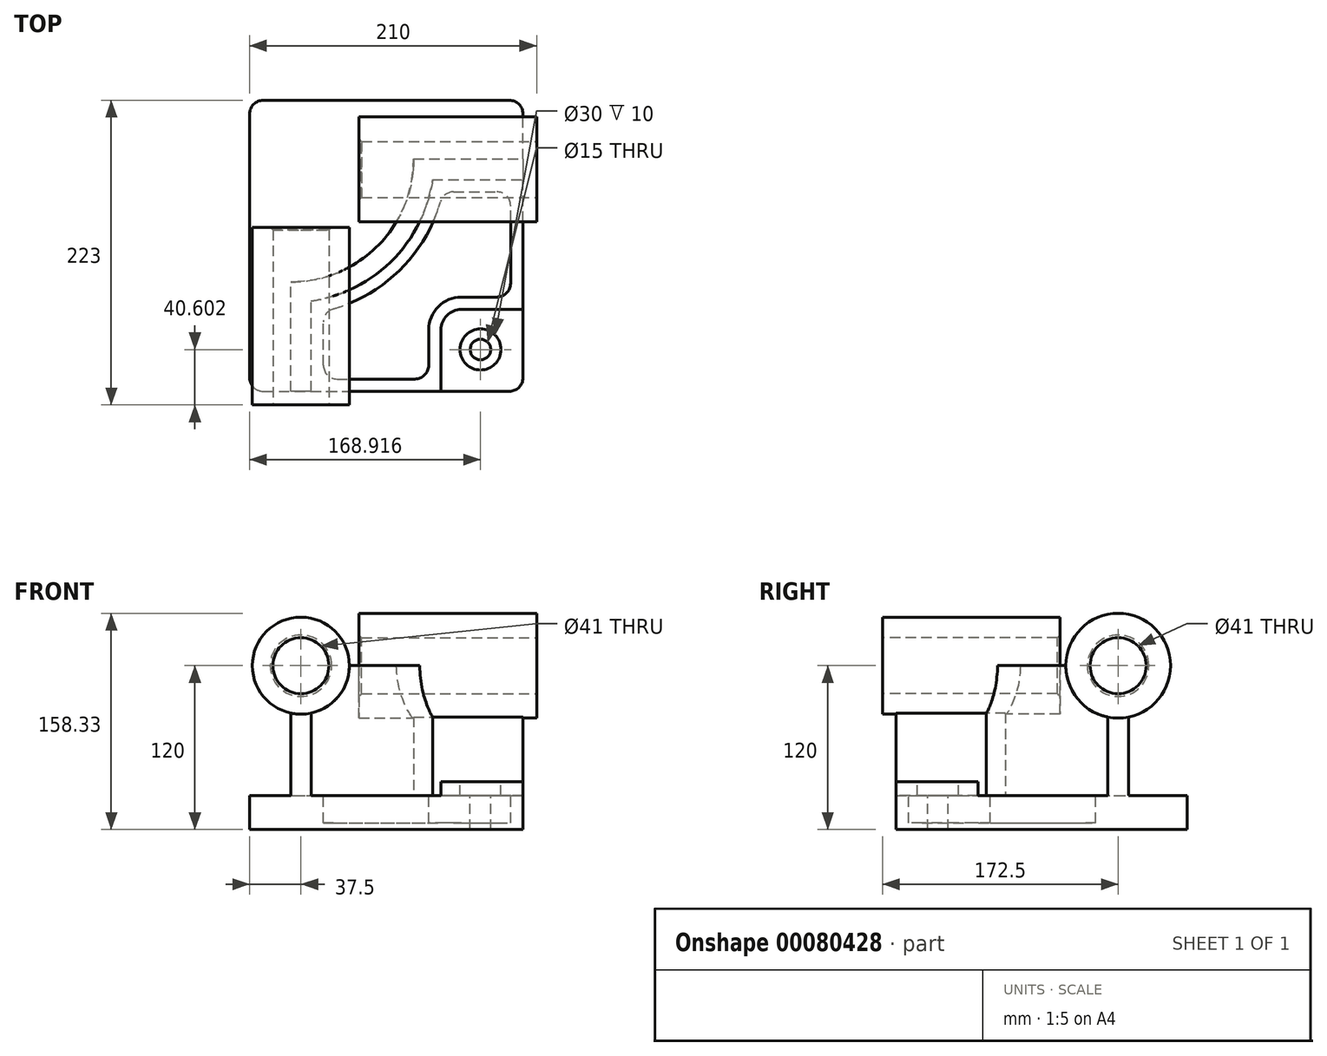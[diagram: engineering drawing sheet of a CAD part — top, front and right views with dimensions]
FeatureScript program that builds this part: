
annotation { "Feature Type Name" : "Feature", "Feature Type Description" : "" }
export const myFeature = defineFeature(function(context is Context, id is Id, definition is map)
    precondition{}
    {
        {
            var Q0;
            Q0=qCreatedBy(makeId("Top.planeOp"),FACE);
            var sketch = newSketch(context, id + "F0", { "sketchPlane" : qUnion([Q0])});
            skLineSegment(sketch, "E0.bottom", {"start": v(0, 0) * mm, "end": v(200, 0) * mm});
            skLineSegment(sketch, "E0.top", {"start": v(0, 213) * mm, "end": v(200, 213) * mm});
            skLineSegment(sketch, "E0.left", {"start": v(0, 0) * mm, "end": v(0, 213) * mm});
            skLineSegment(sketch, "E0.right", {"start": v(200, 0) * mm, "end": v(200, 213) * mm});
            skSolve(sketch);
        }
        {
            var Q0;
            Q0 = qSketchRegion(id + "F0", true);
            extrude(context, id + "F1", {"entities" : qUnion([Q0]), "depth" : 25 * mm});
        }
        {
            var Q0;
            Q0=makeQuery(id+"F1.opExtrude","CAP_FACE",FACE,{"disambiguationData":[OSD([sQuery(id+"F0.wireOp",EDGE,"E0.bottom"),sQuery(id+"F0.wireOp",EDGE,"E0.top"),sQuery(id+"F0.wireOp",EDGE,"E0.left"),sQuery(id+"F0.wireOp",EDGE,"E0.right")])],"isStart":false});
            var sketch = newSketch(context, id + "F2", { "sketchPlane" : qUnion([Q0])});
            skLineSegment(sketch, "E1", {"start": v(30, 0) * mm, "end": v(30, 80) * mm});
            skLineSegment(sketch, "E2", {"start": v(30, 0) * mm, "end": v(45, 0) * mm});
            skLineSegment(sketch, "E3", {"start": v(45, 0) * mm, "end": v(45, 66.08) * mm});
            skLineSegment(sketch, "E4", {"start": v(120, 170) * mm, "end": v(200, 170) * mm});
            skLineSegment(sketch, "E5", {"start": v(133.92, 155) * mm, "end": v(200, 155) * mm});
            skLineSegment(sketch, "E6", {"start": v(200, 155) * mm, "end": v(200, 170) * mm});
            skArc(sketch, "E7", {"start": v(30, 80) * mm, "mid": v(93.64, 106.36) * mm, "end": v(120, 170) * mm});
            skArc(sketch, "E8", {"start": v(45, 66.08) * mm, "mid": v(104.25, 95.75) * mm, "end": v(133.92, 155) * mm});
            skSolve(sketch);
        }
        {
            var Q0;
            Q0 = qSketchRegion(id + "F2", true);
            extrude(context, id + "F3", {"entities" : qUnion([Q0]), "operationType" : NewBodyOperationType.ADD, "depth" : 95 * mm});
        }
        {
            var Q0;
            {var subQ0=sQuery(id+"F0.wireOp",EDGE,"E0.right");var subQ1=sQuery(id+"F0.wireOp",EDGE,"E0.bottom");Q0=makeQuery(id+"F3.boolean.opBoolean","SPLIT",FACE,{"disambiguationData":[TD([makeQuery(id+"F3.opExtrude","SWEPT_FACE",FACE,{"disambiguationData":[OSD([sQuery(id+"F2.wireOp",EDGE,"E3")])]})])],"derivedFrom":makeQuery(id+"F1.opExtrude","CAP_FACE",FACE,{"disambiguationData":[OSD([subQ1,sQuery(id+"F0.wireOp",EDGE,"E0.top"),sQuery(id+"F0.wireOp",EDGE,"E0.left"),subQ0])],"isStart":false})});}
            var sketch = newSketch(context, id + "F4", { "sketchPlane" : qUnion([Q0])});
            skLineSegment(sketch, "E9.bottom", {"start": v(155, 60) * mm, "end": v(200, 60) * mm});
            skLineSegment(sketch, "E9.top", {"start": v(140, 0) * mm, "end": v(200, 0) * mm});
            skLineSegment(sketch, "E9.left", {"start": v(140, 45) * mm, "end": v(140, 0) * mm});
            skLineSegment(sketch, "E9.right", {"start": v(200, 60) * mm, "end": v(200, 0) * mm});
            skPoint(sketch, "E10.visualSharp", {"position": v(140, 60) * mm});
            skArc(sketch, "E10.filletArc", {"start": v(155, 60) * mm, "mid": v(144.4, 55.6) * mm, "end": v(140, 45) * mm});
            skSolve(sketch);
        }
        {
            var Q0;
            Q0 = qSketchRegion(id + "F4", true);
            extrude(context, id + "F5", {"entities" : qUnion([Q0]), "operationType" : NewBodyOperationType.ADD, "depth" : 10 * mm});
        }
        {
            var Q0;
            Q0=makeQuery(id+"F5.opExtrude","CAP_FACE",FACE,{"disambiguationData":[OSD([sQuery(id+"F4.wireOp",EDGE,"E9.bottom"),sQuery(id+"F4.wireOp",EDGE,"E9.top"),sQuery(id+"F4.wireOp",EDGE,"E9.left"),sQuery(id+"F4.wireOp",EDGE,"E9.right"),sQuery(id+"F4.wireOp",EDGE,"E10.filletArc")])],"isStart":false});
            var sketch = newSketch(context, id + "F6", { "sketchPlane" : qUnion([Q0])});
            skCircle(sketch, "E11", {"center": v(168.92, 30.6) * mm, "radius": 15 * mm});
            skSolve(sketch);
        }
        {
            var Q0;
            Q0 = qSketchRegion(id + "F6", true);
            extrude(context, id + "F7", {"entities" : qUnion([Q0]), "operationType" : NewBodyOperationType.REMOVE, "oppositeDirection" : true, "depth" : 10 * mm});
        }
        {
            var Q0;
            Q0=makeQuery(id+"F7.boolean.opBoolean","COPY",FACE,{"derivedFrom":makeQuery(id+"F7.opExtrude","CAP_FACE",FACE,{"disambiguationData":[OSD([sQuery(id+"F6.wireOp",EDGE,"E11")])],"isStart":false})});
            var sketch = newSketch(context, id + "F8", { "sketchPlane" : qUnion([Q0])});
            skCircle(sketch, "E12", {"center": v(168.92, 30.6) * mm, "radius": 7.5 * mm});
            skSolve(sketch);
        }
        {
            var Q0;
            Q0 = qSketchRegion(id + "F8", true);
            extrude(context, id + "F9", {"entities" : qUnion([Q0]), "operationType" : NewBodyOperationType.REMOVE, "endBound" : BoundingType.THROUGH_ALL, "oppositeDirection" : true, "depth" : 25 * mm});
        }
        {
            var Q0;
            {var subQ0=sQuery(id+"F0.wireOp",EDGE,"E0.right");var subQ1=sQuery(id+"F0.wireOp",EDGE,"E0.bottom");Q0=makeQuery(id+"F3.boolean.opBoolean","SPLIT",FACE,{"disambiguationData":[TD([makeQuery(id+"F3.opExtrude","SWEPT_FACE",FACE,{"disambiguationData":[OSD([sQuery(id+"F2.wireOp",EDGE,"E3")])]})])],"derivedFrom":makeQuery(id+"F1.opExtrude","CAP_FACE",FACE,{"disambiguationData":[OSD([subQ1,sQuery(id+"F0.wireOp",EDGE,"E0.top"),sQuery(id+"F0.wireOp",EDGE,"E0.left"),subQ0])],"isStart":false})});}
            var sketch = newSketch(context, id + "F10", { "sketchPlane" : qUnion([Q0])});
            skLineSegment(sketch, "E13.0", {"start": v(149.25, 146) * mm, "end": v(181, 146) * mm});
            skArc(sketch, "E13.1", {"start": v(61.26, 60.37) * mm, "mid": v(110.61, 89.39) * mm, "end": v(139.63, 138.74) * mm});
            skLineSegment(sketch, "E13.2", {"start": v(54, 19) * mm, "end": v(54, 50.75) * mm});
            skLineSegment(sketch, "E14", {"start": v(64, 9) * mm, "end": v(121, 9) * mm});
            skLineSegment(sketch, "E15", {"start": v(191, 79) * mm, "end": v(191, 136) * mm});
            skLineSegment(sketch, "E16.0", {"start": v(155, 69) * mm, "end": v(181, 69) * mm});
            skArc(sketch, "E16.1", {"start": v(155, 69) * mm, "mid": v(138.03, 61.97) * mm, "end": v(131, 45) * mm});
            skLineSegment(sketch, "E16.2", {"start": v(131, 45) * mm, "end": v(131, 19) * mm});
            skPoint(sketch, "E17.visualSharp", {"position": v(54, 58.55) * mm});
            skArc(sketch, "E17.filletArc", {"start": v(61.26, 60.37) * mm, "mid": v(56.02, 56.78) * mm, "end": v(54, 50.75) * mm});
            skPoint(sketch, "E18.visualSharp", {"position": v(54, 9) * mm});
            skArc(sketch, "E18.filletArc", {"start": v(54, 19) * mm, "mid": v(56.93, 11.93) * mm, "end": v(64, 9) * mm});
            skPoint(sketch, "E19.visualSharp", {"position": v(131, 9) * mm});
            skArc(sketch, "E19.filletArc", {"start": v(121, 9) * mm, "mid": v(128.07, 11.93) * mm, "end": v(131, 19) * mm});
            skPoint(sketch, "E20.visualSharp", {"position": v(191, 69) * mm});
            skArc(sketch, "E20.filletArc", {"start": v(181, 69) * mm, "mid": v(188.07, 71.93) * mm, "end": v(191, 79) * mm});
            skPoint(sketch, "E21.visualSharp", {"position": v(191, 146) * mm});
            skArc(sketch, "E21.filletArc", {"start": v(191, 136) * mm, "mid": v(188.07, 143.07) * mm, "end": v(181, 146) * mm});
            skPoint(sketch, "E22.visualSharp", {"position": v(141.45, 146) * mm});
            skArc(sketch, "E22.filletArc", {"start": v(149.25, 146) * mm, "mid": v(143.22, 143.98) * mm, "end": v(139.63, 138.74) * mm});
            skSolve(sketch);
        }
        {
            var Q0;
            Q0 = qSketchRegion(id + "F10", true);
            extrude(context, id + "F11", {"entities" : qUnion([Q0]), "operationType" : NewBodyOperationType.REMOVE, "oppositeDirection" : true, "depth" : 20 * mm});
        }
        {
            var Q0;
            Q0=makeQuery(id+"F5.boolean.opBoolean","MERGE",FACE,{"derivedFrom":[makeQuery(id+"F3.boolean.opBoolean","MERGE",FACE,{"derivedFrom":[makeQuery(id+"F1.opExtrude","SWEPT_FACE",FACE,{"disambiguationData":[OSD([sQuery(id+"F0.wireOp",EDGE,"E0.bottom")])]}),makeQuery(id+"F3.opExtrude","SWEPT_FACE",FACE,{"disambiguationData":[OSD([sQuery(id+"F2.wireOp",EDGE,"E2")])]})]}),makeQuery(id+"F5.opExtrude","SWEPT_FACE",FACE,{"disambiguationData":[OSD([sQuery(id+"F4.wireOp",EDGE,"E9.top")])]})]});
            cPlane(context, id + "F12", {"entities" : qUnion([Q0]), "cplaneType" : CPlaneType.OFFSET, "offset" : 10 * mm, "width" : 150 * mm, "height" : 150 * mm});
        }
        {
            var Q0;
            Q0=qCreatedBy(id+"F12.planeOp",FACE);
            var sketch = newSketch(context, id + "F13", { "sketchPlane" : qUnion([Q0])});
            skCircle(sketch, "E23", {"center": v(37.5, 120) * mm, "radius": 35.5 * mm});
            skSolve(sketch);
        }
        {
            var Q0;
            Q0 = qSketchRegion(id + "F13", true);
            extrude(context, id + "F14", {"entities" : qUnion([Q0]), "operationType" : NewBodyOperationType.ADD, "oppositeDirection" : true, "depth" : 130 * mm});
        }
        {
            var Q0;
            Q0=makeQuery(id+"F13.imprint","IMPRINT",FACE,{"disambiguationData":[TD([[makeQuery(id+"F13.imprint","IMPRINT",EDGE,{"derivedFrom":sQuery(id+"F13.wireOp",EDGE,"E23")}),1.0]])]});
            var sketch = newSketch(context, id + "F15", { "sketchPlane" : qUnion([Q0])});
            skCircle(sketch, "E24", {"center": v(37.5, 120) * mm, "radius": 20.5 * mm});
            skSolve(sketch);
        }
        {
            var Q0;
            Q0 = qSketchRegion(id + "F15", true);
            extrude(context, id + "F16", {"entities" : qUnion([Q0]), "operationType" : NewBodyOperationType.REMOVE, "endBound" : BoundingType.THROUGH_ALL, "oppositeDirection" : true, "depth" : 25 * mm});
        }
        {
            var Q0;
            Q0=makeQuery(id+"F5.boolean.opBoolean","MERGE",FACE,{"derivedFrom":[makeQuery(id+"F3.boolean.opBoolean","MERGE",FACE,{"derivedFrom":[makeQuery(id+"F1.opExtrude","SWEPT_FACE",FACE,{"disambiguationData":[OSD([sQuery(id+"F0.wireOp",EDGE,"E0.right")])]}),makeQuery(id+"F3.opExtrude","SWEPT_FACE",FACE,{"disambiguationData":[OSD([sQuery(id+"F2.wireOp",EDGE,"E6")])]})]}),makeQuery(id+"F5.opExtrude","SWEPT_FACE",FACE,{"disambiguationData":[OSD([sQuery(id+"F4.wireOp",EDGE,"E9.right")])]})]});
            cPlane(context, id + "F17", {"entities" : qUnion([Q0]), "cplaneType" : CPlaneType.OFFSET, "offset" : 10 * mm, "width" : 150 * mm, "height" : 150 * mm});
        }
        {
            var Q0;
            Q0=qCreatedBy(id+"F17.planeOp",FACE);
            var sketch = newSketch(context, id + "F18", { "sketchPlane" : qUnion([Q0])});
            skCircle(sketch, "E25", {"center": v(162.5, 120) * mm, "radius": 38.33 * mm});
            skSolve(sketch);
        }
        {
            var Q0;
            Q0 = qSketchRegion(id + "F18", true);
            extrude(context, id + "F19", {"entities" : qUnion([Q0]), "operationType" : NewBodyOperationType.ADD, "oppositeDirection" : true, "depth" : 130 * mm});
        }
        {
            var Q0;
            Q0=makeQuery(id+"F19.opExtrude","CAP_FACE",FACE,{"disambiguationData":[OSD([sQuery(id+"F18.wireOp",EDGE,"E25")])],"isStart":true});
            var sketch = newSketch(context, id + "F20", { "sketchPlane" : qUnion([Q0])});
            skCircle(sketch, "E26", {"center": v(162.5, 120) * mm, "radius": 20.5 * mm});
            skSolve(sketch);
        }
        {
            var Q0;
            Q0 = qSketchRegion(id + "F20", true);
            extrude(context, id + "F21", {"entities" : qUnion([Q0]), "operationType" : NewBodyOperationType.REMOVE, "endBound" : BoundingType.THROUGH_ALL, "oppositeDirection" : true, "depth" : 25 * mm});
        }
        {
            var Q0;
            Q0=makeQuery(id+"F1.opExtrude","SWEPT_EDGE",EDGE,{"disambiguationData":[OSD([sQuery(id+"F0.wireOp",EDGE,"E0.bottom"),sQuery(id+"F0.wireOp",EDGE,"E0.left")])]});
            var Q1;
            Q1=makeQuery(id+"F5.boolean.opBoolean","MERGE",EDGE,{"derivedFrom":[makeQuery(id+"F1.opExtrude","SWEPT_EDGE",EDGE,{"disambiguationData":[OSD([sQuery(id+"F0.wireOp",EDGE,"E0.bottom"),sQuery(id+"F0.wireOp",EDGE,"E0.right")])]}),makeQuery(id+"F5.opExtrude","SWEPT_EDGE",EDGE,{"disambiguationData":[OSD([sQuery(id+"F4.wireOp",EDGE,"E9.top"),sQuery(id+"F4.wireOp",EDGE,"E9.right")])]})]});
            var Q2;
            Q2=makeQuery(id+"F1.opExtrude","SWEPT_EDGE",EDGE,{"disambiguationData":[OSD([sQuery(id+"F0.wireOp",EDGE,"E0.top"),sQuery(id+"F0.wireOp",EDGE,"E0.right")])]});
            var Q3;
            Q3=makeQuery(id+"F1.opExtrude","SWEPT_EDGE",EDGE,{"disambiguationData":[OSD([sQuery(id+"F0.wireOp",EDGE,"E0.top"),sQuery(id+"F0.wireOp",EDGE,"E0.left")])]});
            fillet(context, id + "F22", {"entities" : qUnion([Q0, Q1, Q2, Q3]), "radius" : 10 * mm, "tangentPropagation" : true, "allowEdgeOverflow" : false});
        }
        {
            var Q0;
            Q0=makeQuery(id+"F16.boolean.opBoolean","COPY",EDGE,{"derivedFrom":makeQuery(id+"F16.opExtrude","CAP_EDGE",EDGE,{"disambiguationData":[OSD([sQuery(id+"F15.wireOp",EDGE,"E24")])],"isStart":true})});
            var Q1;
            Q1=makeQuery(id+"F21.boolean.opBoolean","COPY",EDGE,{"derivedFrom":makeQuery(id+"F21.opExtrude","CAP_EDGE",EDGE,{"disambiguationData":[OSD([sQuery(id+"F20.wireOp",EDGE,"E26")])],"isStart":true})});
            var Q2;
            Q2=makeQuery(id+"F16.boolean.opBoolean","INTERSECT",EDGE,{"derivedFrom":[makeQuery(id+"F14.opExtrude","CAP_FACE",FACE,{"disambiguationData":[OSD([sQuery(id+"F13.wireOp",EDGE,"E23")])],"isStart":false}),makeQuery(id+"F16.opExtrude","SWEPT_FACE",FACE,{"disambiguationData":[OSD([sQuery(id+"F15.wireOp",EDGE,"E24")])]})]});
            var Q3;
            Q3=makeQuery(id+"F21.boolean.opBoolean","INTERSECT",EDGE,{"derivedFrom":[makeQuery(id+"F19.opExtrude","CAP_FACE",FACE,{"disambiguationData":[OSD([sQuery(id+"F18.wireOp",EDGE,"E25")])],"isStart":false}),makeQuery(id+"F21.opExtrude","SWEPT_FACE",FACE,{"disambiguationData":[OSD([sQuery(id+"F20.wireOp",EDGE,"E26")])]})]});
            chamfer(context, id + "F23", {"entities" : qUnion([Q0, Q1, Q2, Q3]), "chamferType" : ChamferType.OFFSET_ANGLE, "width" : 2 * mm, "oppositeDirection" : false, "angle" : 45 * degree, "tangentPropagation" : true});
        }
    });
